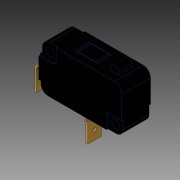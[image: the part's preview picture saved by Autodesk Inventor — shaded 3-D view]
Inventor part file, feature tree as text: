
AUTODESK INVENTOR PART (.ipt)
format: ipt  version: 2016 SP1 (Build 200210100, 210)  size: 245,248 bytes
history: native  units: in
note: dims shown in document units (in); Inventor stores cm internally (conversion verified against a paired STEP export)
features: extrude x3, sketch x3, mirror x2, plane x1, fillet x1
ambient origin geometry x8: Origin, YZ Plane, XZ Plane, XY Plane, X Axis, Y Axis, Z Axis, Center Point
bodies: Solid1 (feature_tree)
feature tree (10):
  extrude  "Extrusion1"  Depth=0.0197in
  plane  "Work Plane1"
  mirror  "Mirror1"
  extrude  "Extrusion2"  Depth=0.0472in
  mirror  "Mirror2"
  extrude  "Extrusion4"  Depth=0.0197in TaperAngle=0.0deg
  sketch  "Sketch1"  dims[d1=0.0197in d2=0.0in d5=0.0472in]
  sketch  "Sketch2"  dims[d6=0.0472in d7=0.0472in]
  sketch  "Sketch3"  dims[d8=0.0472in d9=0.0197in d10=0.0in d12=0.1969in d15=0.0079in d16=0.0079in d17=0.0394in d18=0.0197in d19=0.0in]
  fillet  "Fillet1"  Radius=0.1969in
